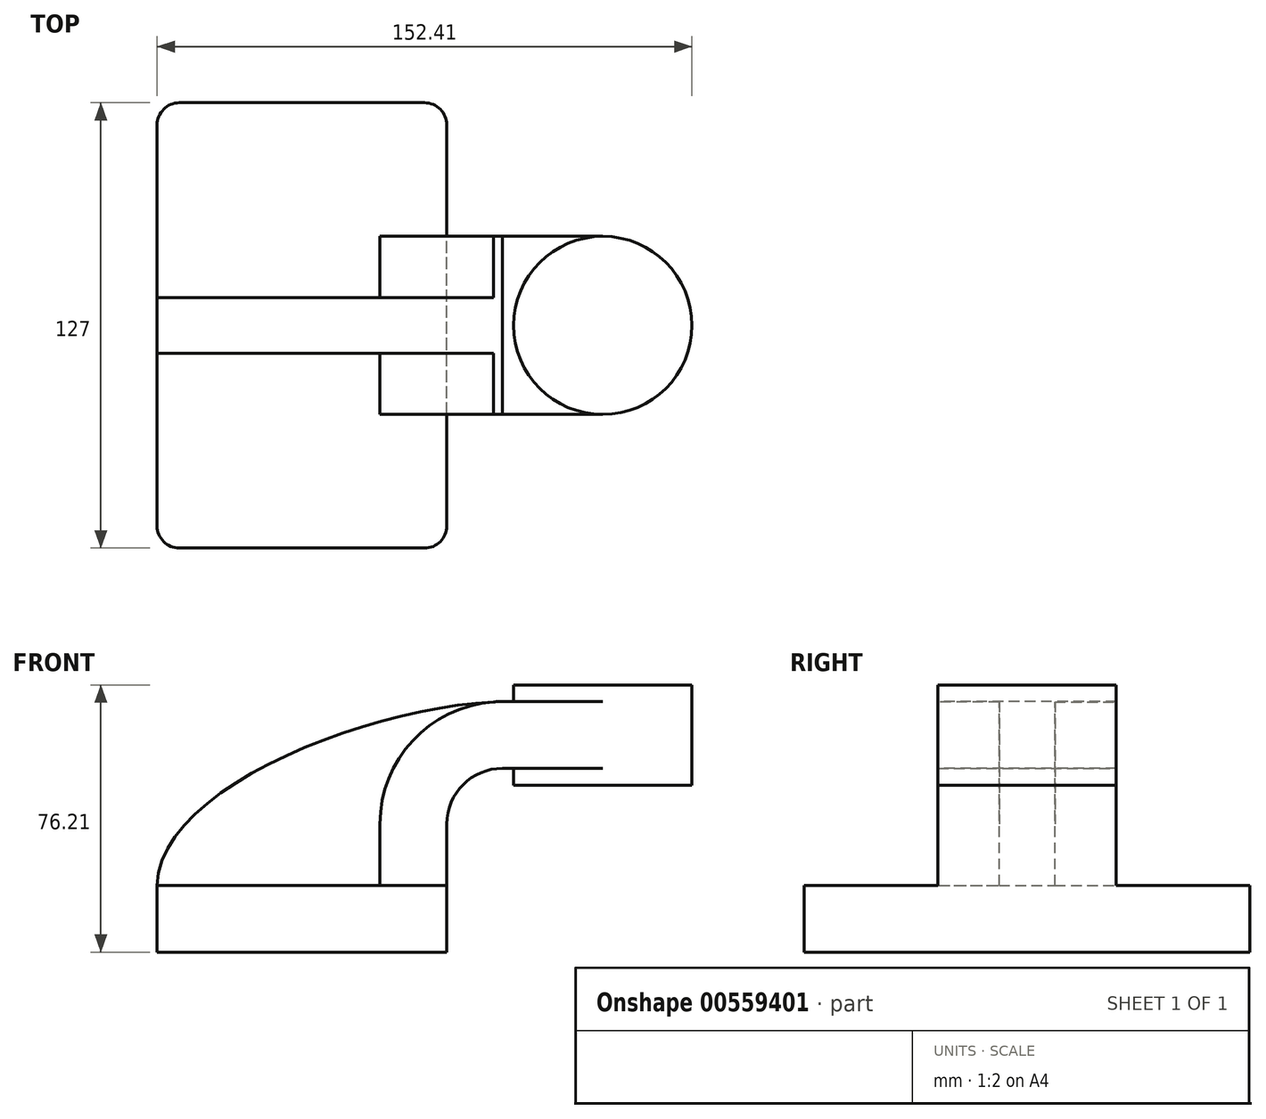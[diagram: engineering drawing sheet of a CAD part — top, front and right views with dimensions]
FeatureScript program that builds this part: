
annotation { "Feature Type Name" : "Feature", "Feature Type Description" : "" }
export const myFeature = defineFeature(function(context is Context, id is Id, definition is map)
    precondition{}
    {
        {
            var Q0;
            Q0=qCreatedBy(makeId("Front.planeOp"),FACE);
            var sketch = newSketch(context, id + "F0", { "sketchPlane" : qUnion([Q0])});
            skLineSegment(sketch, "E0.bottom", {"start": v(-41.28, -9.53) * mm, "end": v(41.28, -9.53) * mm});
            skLineSegment(sketch, "E0.top", {"start": v(-41.28, 9.53) * mm, "end": v(41.28, 9.53) * mm});
            skLineSegment(sketch, "E0.left", {"start": v(-41.28, -9.53) * mm, "end": v(-41.28, 9.53) * mm});
            skLineSegment(sketch, "E0.right", {"start": v(41.28, -9.53) * mm, "end": v(41.28, 9.52) * mm});
            skPoint(sketch, "E0.middle", {"position": v(0, 0) * mm});
            skLineSegment(sketch, "E1.bottom", {"start": v(111.12, 38.1) * mm, "end": v(60.33, 38.1) * mm});
            skLineSegment(sketch, "E1.top", {"start": v(111.13, 66.67) * mm, "end": v(60.33, 66.67) * mm});
            skLineSegment(sketch, "E1.left", {"start": v(111.12, 38.1) * mm, "end": v(111.12, 66.67) * mm});
            skLineSegment(sketch, "E1.right", {"start": v(60.33, 38.1) * mm, "end": v(60.33, 66.67) * mm});
            skPoint(sketch, "E1.middle", {"position": v(85.73, 52.39) * mm});
            skLineSegment(sketch, "E2", {"start": v(41.27, 9.53) * mm, "end": v(41.27, 27) * mm});
            skArc(sketch, "E3", {"start": v(41.27, 27) * mm, "mid": v(45.92, 38.23) * mm, "end": v(57.15, 42.88) * mm});
            skLineSegment(sketch, "E4", {"start": v(57.15, 42.88) * mm, "end": v(85.73, 42.88) * mm});
            skLineSegment(sketch, "E5.0", {"start": v(57.15, 61.93) * mm, "end": v(85.73, 61.93) * mm});
            skArc(sketch, "E5.1", {"start": v(22.23, 27) * mm, "mid": v(32.45, 51.7) * mm, "end": v(57.15, 61.93) * mm});
            skLineSegment(sketch, "E5.2", {"start": v(22.22, 9.53) * mm, "end": v(22.22, 27) * mm});
            skLineSegment(sketch, "E6", {"start": v(85.73, 66.67) * mm, "end": v(85.72, 38.1) * mm});
            skFitSpline(sketch, "E7", {"points": [v(-41.28, 9.53) * mm, v(57.15, 61.93) * mm], "startDerivative": vector(1.48, 84.23) * mm, "endDerivative": vector(110.28, 2.6) * mm});
            skSolve(sketch);
        }
        {
            var Q0;
            Q0=makeQuery(id+"F0.imprint","IMPRINT",FACE,{"disambiguationData":[TD([[makeQuery(id+"F0.imprint","IMPRINT",EDGE,{"derivedFrom":sQuery(id+"F0.wireOp",EDGE,"E0.bottom")}),1.0]])]});
            extrude(context, id + "F1", {"entities" : qUnion([Q0]), "endBound" : BoundingType.SYMMETRIC, "depth" : 127 * mm, "offsetDistance" : 25.4 * mm});
        }
        {
            var Q0;
            {var subQ1=sQuery(id+"F0.wireOp",EDGE,"E2");Q0=makeQuery(id+"F0.imprint","IMPRINT",FACE,{"disambiguationData":[TD([[makeQuery(id+"F0.imprint","IMPRINT",EDGE,{"derivedFrom":subQ1}),1.0]])]});}
            var Q1;
            {var subQ0=sQuery(id+"F0.wireOp",EDGE,"E4");var subQ1=sQuery(id+"F0.wireOp",EDGE,"E1.right");var subQ2=makeQuery(id+"F0.imprint","INTERSECT",VERTEX,{"derivedFrom":[subQ1,subQ0]});Q1=makeQuery(id+"F0.imprint","IMPRINT",FACE,{"disambiguationData":[TD([[makeQuery(id+"F0.imprint","IMPRINT",EDGE,{"disambiguationData":[TD([[subQ2,-1.0]])],"derivedFrom":subQ1}),-1.0]])]});}
            extrude(context, id + "F2", {"entities" : qUnion([Q0, Q1]), "operationType" : NewBodyOperationType.ADD, "endBound" : BoundingType.SYMMETRIC, "depth" : 50.8 * mm, "offsetDistance" : 25.4 * mm});
        }
        {
            var Q0;
            {var subQ3=sQuery(id+"F0.wireOp",EDGE,"E5.2");Q0=makeQuery(id+"F0.imprint","IMPRINT",FACE,{"disambiguationData":[TD([[makeQuery(id+"F0.imprint","IMPRINT",EDGE,{"derivedFrom":subQ3}),1.0]])]});}
            extrude(context, id + "F3", {"entities" : qUnion([Q0]), "operationType" : NewBodyOperationType.ADD, "endBound" : BoundingType.SYMMETRIC, "depth" : 15.88 * mm, "offsetDistance" : 25.4 * mm});
        }
        {
            var Q0;
            {var subQ0=sQuery(id+"F0.wireOp",EDGE,"E1.left");Q0=makeQuery(id+"F0.imprint","IMPRINT",FACE,{"disambiguationData":[TD([[makeQuery(id+"F0.imprint","IMPRINT",EDGE,{"derivedFrom":subQ0}),1.0]])]});}
            var Q1;
            Q1=sQuery(id+"F0.wireOp",EDGE,"E6");
            revolve(context, id + "F4", {"operationType" : NewBodyOperationType.ADD, "entities" : qUnion([Q0]), "axis" : qUnion([Q1]), "revolveType" : RevolveType.FULL});
        }
        {
            var Q0;
            Q0=makeQuery(id+"F1.opExtrude","CAP_EDGE",EDGE,{"disambiguationData":[OSD([sQuery(id+"F0.wireOp",EDGE,"E0.right")])],"isStart":false});
            var Q1;
            Q1=makeQuery(id+"F1.opExtrude","CAP_EDGE",EDGE,{"disambiguationData":[OSD([sQuery(id+"F0.wireOp",EDGE,"E0.right")])],"isStart":true});
            var Q2;
            Q2=makeQuery(id+"F1.opExtrude","CAP_EDGE",EDGE,{"disambiguationData":[OSD([sQuery(id+"F0.wireOp",EDGE,"E0.left")])],"isStart":true});
            var Q3;
            Q3=makeQuery(id+"F1.opExtrude","CAP_EDGE",EDGE,{"disambiguationData":[OSD([sQuery(id+"F0.wireOp",EDGE,"E0.left")])],"isStart":false});
            fillet(context, id + "F5", {"entities" : qUnion([Q0, Q1, Q2, Q3]), "radius" : 6.35 * mm, "tangentPropagation" : true, "allowEdgeOverflow" : false});
        }
    });
